AUTODESK INVENTOR PART (.ipt)
format: ipt  version: 2024.3 (Build 283343000, 343)  size: 212,480 bytes
history: native  units: mm (DEFAULTED — no unit token found)
features: other x4, sketch x4, extrude x3, plane x2, split x1
ambient origin geometry x8: Origin, YZ Plane, XZ Plane, XY Plane, X Axis, Y Axis, Z Axis, Center Point
bodies: Solid1 (feature_tree), Body (feature_tree)
feature tree (14):
  parser-record x1  (decoder bookkeeping rows leaked as tree rows — omitted from the tree; the rows remain in map.json)
  other  "Driven Length"
  other  "Start Plane"
  other  "End Plane"
  extrude  "Extrusion2"  TaperAngle=0.0deg  [1 undecoded]
  extrude  "Extrusion3"  Depth=100.0mm
  plane  "Work Plane5"
  split  "Split2"
  extrude  "Extrusion4"  Depth=3.0mm
  sketch  "Sketch3"  dims[d3=450.0mm d4=0.0mm]
  plane  "Work Plane3"
  sketch  "Sketch5"  dims[d7=6.0mm d9=100.0mm]
  sketch  "Sketch6"  dims[d11=100.0mm d12=3.0mm]
  sketch  "Sketch7"  dims[d13=-0.0mm d14=450.0mm d15=50.0mm d16=50.0mm d17=90.0deg d18=450.0mm d19=141.42mm d20=10.0mm d21=0.0mm d22=2.0mm d23=2.0mm d24=20.0mm d25=20.0mm d26=2.0mm d27=2.0mm d28=20.0mm d29=20.0mm d30=100.0mm d31=0.0mm d32=97.42mm d33=5.0mm d34=0.0mm]
note: 1 required parameter value undecoded (feature->parameter linkage not recoverable at this tier; creation-order binding heuristic only, values carry confidence <= 0.55)
